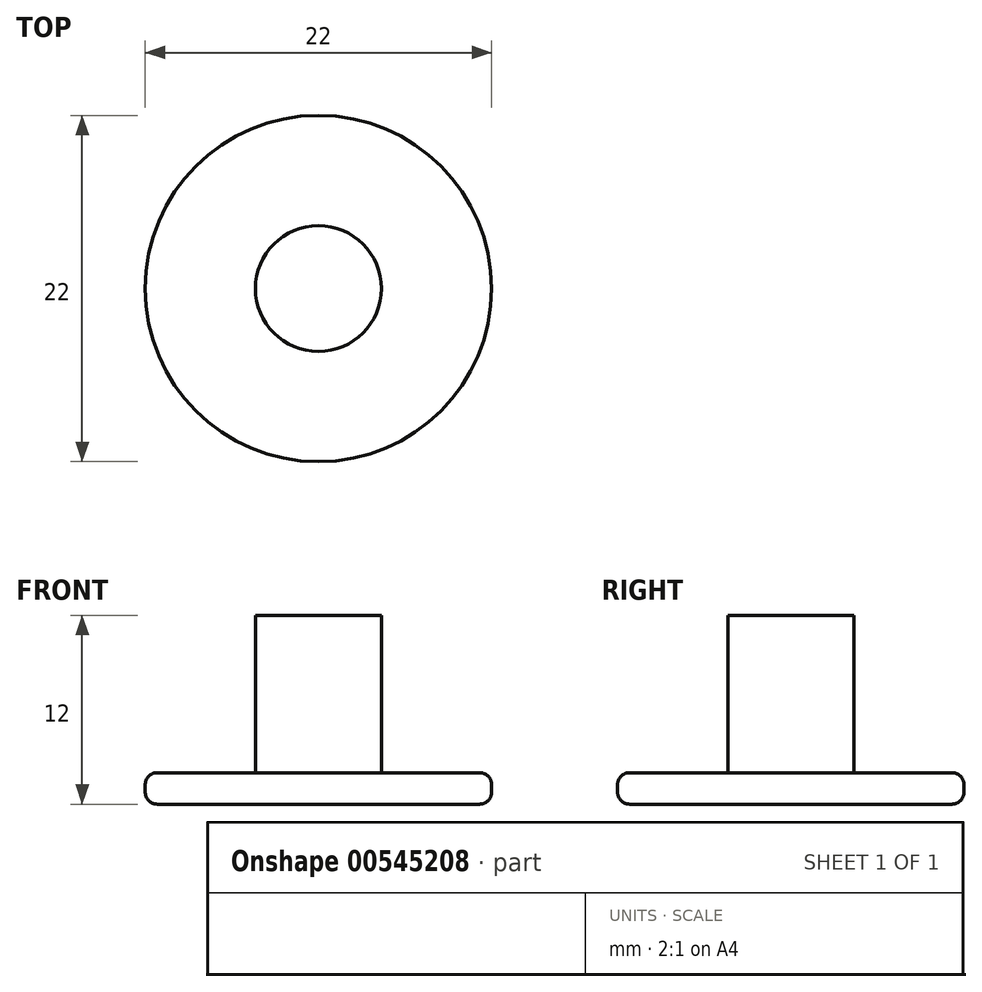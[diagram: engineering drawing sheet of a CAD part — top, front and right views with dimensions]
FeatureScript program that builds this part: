
annotation { "Feature Type Name" : "Feature", "Feature Type Description" : "" }
export const myFeature = defineFeature(function(context is Context, id is Id, definition is map)
    precondition{}
    {
        {
            var Q0;
            Q0=qCreatedBy(makeId("Top.planeOp"),FACE);
            var sketch = newSketch(context, id + "F0", { "sketchPlane" : qUnion([Q0])});
            skCircle(sketch, "E0", {"center": v(0, 0) * mm, "radius": 11 * mm});
            skSolve(sketch);
        }
        {
            var Q0;
            Q0 = qSketchRegion(id + "F0", true);
            extrude(context, id + "F1", {"entities" : qUnion([Q0]), "depth" : 2 * mm, "offsetDistance" : 25.4 * mm});
        }
        {
            var Q0;
            Q0=qCreatedBy(makeId("Top.planeOp"),FACE);
            var sketch = newSketch(context, id + "F2", { "sketchPlane" : qUnion([Q0])});
            skCircle(sketch, "E1", {"center": v(0, 0) * mm, "radius": 4 * mm});
            skSolve(sketch);
        }
        {
            var Q0;
            Q0=makeQuery(id+"F2.imprint","IMPRINT",FACE,{"disambiguationData":[TD([[makeQuery(id+"F2.imprint","IMPRINT",EDGE,{"derivedFrom":sQuery(id+"F2.wireOp",EDGE,"E1")}),1.0]])]});
            extrude(context, id + "F3", {"entities" : qUnion([Q0]), "operationType" : NewBodyOperationType.ADD, "depth" : 12 * mm, "offsetDistance" : 25.4 * mm});
        }
        {
            var Q0;
            Q0=makeQuery(id+"F1.opExtrude","CAP_EDGE",EDGE,{"disambiguationData":[OSD([sQuery(id+"F0.wireOp",EDGE,"E0")])],"isStart":false});
            var Q1;
            Q1=makeQuery(id+"F1.opExtrude","SWEPT_FACE",FACE,{"disambiguationData":[OSD([sQuery(id+"F0.wireOp",EDGE,"E0")])]});
            fillet(context, id + "F4", {"entities" : qUnion([Q0, Q1]), "radius" : 0.76 * mm, "tangentPropagation" : true, "allowEdgeOverflow" : false});
        }
    });
